# Revit family: Moon
name_source: partatom
category: Mechanical Equipment
units: mm (PartAtom-declared; Revit-internal decimal feet)

## family parameters
Always vertical = Yes
Classification = None
Cut with Voids When Loaded = No
Part Type = Normal
Room Calculation Point = No
Round Connector Dimension = Use Diameter
Shared = No
Work Plane-Based = No

## types (2) — shared parameters
00_20_Manufacturer = Blauberg
00_20_Name = Axial fan
Amperage = 0 A
Casing Material = Plastic, opaque, white
Description = For round channels
Frequency = 50 Hz
H = 180 mm  [stored 0.590551 ft]
Height = 180 mm  [stored 0.590551 ft]
Load Classification = HVAC
Maintenance zone material = <By Category>
Manufacturer = Blauberg
Number of Fase = 1
URL = https://blaubergventilatoren.de
Voltage = 230 V
Width = 180 mm  [stored 0.590551 ft]
a = 180 mm  [stored 0.590551 ft]
zero-valued in all types: Default Elevation

## per-type parameters (varying)
| type | Apparent Load | Diameter | Dy | Length | Power | Sound pressure level at 3 m distance | Weight | c | d | e |
| Moon 100 | 12 W | 99 mm  [stored 0.324803 ft] | 95 mm  [stored 0.31168 ft] | 117 mm  [stored 0.383858 ft] | 8 W | 27 dBA | 0.51 kg | 79 mm | 99 mm  [stored 0.324803 ft] | 38 mm  [stored 0.124672 ft] |
| Moon 125 | 25 W | 124 mm  [stored 0.406824 ft] | 120 mm  [stored 0.393701 ft] | 130 mm  [stored 0.426509 ft] | 18 W | 32 dBA | 0.75 kg | 85 mm  [stored 0.278871 ft] | 124 mm  [stored 0.406824 ft] | 45 mm  [stored 0.147638 ft] |

note: column(s) folded — value = type name in every type: 00_20_Type

note: [stored X ft] marks values corroborated as IEEE doubles in the binary element streams (Revit-internal decimal feet)
